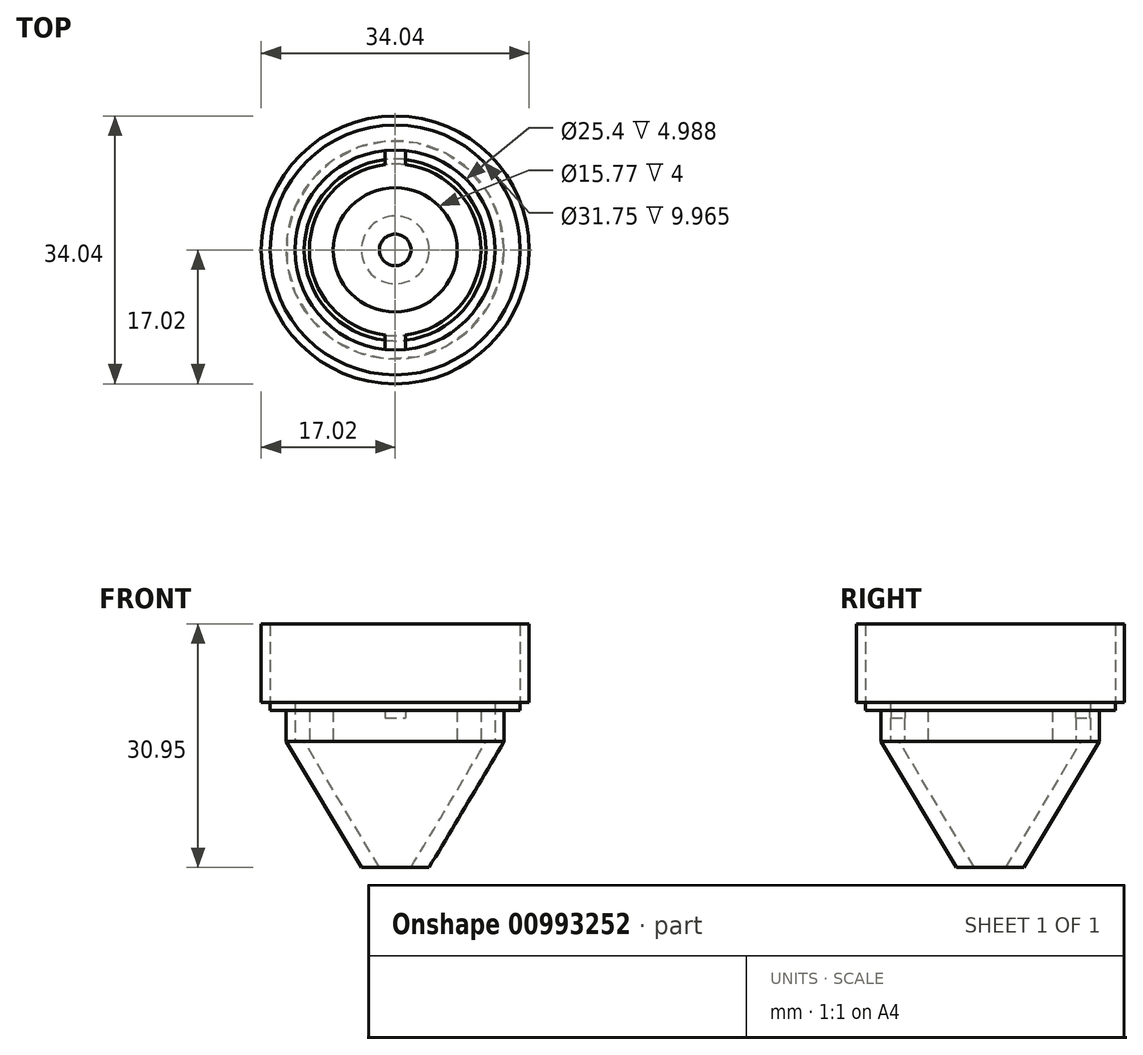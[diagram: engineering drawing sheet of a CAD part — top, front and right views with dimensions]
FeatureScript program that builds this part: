
annotation { "Feature Type Name" : "Feature", "Feature Type Description" : "" }
export const myFeature = defineFeature(function(context is Context, id is Id, definition is map)
    precondition{}
    {
        {
            var Q0;
            Q0=qCreatedBy(makeId("Top.planeOp"),FACE);
            var sketch = newSketch(context, id + "F0", { "sketchPlane" : qUnion([Q0])});
            skCircle(sketch, "E0", {"center": v(0, 0) * mm, "radius": 7.89 * mm});
            skArc(sketch, "E1", {"start": v(1.3, -10.82) * mm, "mid": v(10.9, 0) * mm, "end": v(1.3, 10.82) * mm});
            skArc(sketch, "E2", {"start": v(1.3, -12.63) * mm, "mid": v(12.7, 0) * mm, "end": v(1.3, 12.63) * mm});
            skCircle(sketch, "E3", {"center": v(0, 0) * mm, "radius": 13.85 * mm});
            skLineSegment(sketch, "E4", {"start": v(-1.3, -12.63) * mm, "end": v(-1.3, -10.82) * mm});
            skLineSegment(sketch, "E5.MirrorCS", {"start": v(1.3, -12.63) * mm, "end": v(1.3, -10.82) * mm});
            skLineSegment(sketch, "E6.trimOffspring", {"start": v(-1.3, 10.82) * mm, "end": v(-1.3, 12.63) * mm});
            skLineSegment(sketch, "E7.trimOffspring", {"start": v(1.3, 10.82) * mm, "end": v(1.3, 12.63) * mm});
            skArc(sketch, "E8.trimOffspring", {"start": v(-1.3, 10.82) * mm, "mid": v(-10.9, 0) * mm, "end": v(-1.3, -10.82) * mm});
            skArc(sketch, "E9.trimOffspring", {"start": v(-1.3, 12.63) * mm, "mid": v(-12.7, 0) * mm, "end": v(-1.3, -12.63) * mm});
            skSolve(sketch);
        }
        {
            var Q0;
            Q0=qSketchRegion(id+"F0",true);
            extrude(context, id + "F1", {"entities" : qUnion([Q0]), "depth" : 4 * mm, "offsetDistance" : 25.4 * mm});
        }
        {
            var Q0;
            Q0=qCreatedBy(makeId("Top.planeOp"),FACE);
            var sketch = newSketch(context, id + "F2", { "sketchPlane" : qUnion([Q0])});
            skCircle(sketch, "E10", {"center": v(0, 0) * mm, "radius": 12.7 * mm});
            skCircle(sketch, "E11", {"center": v(0, 0) * mm, "radius": 10.9 * mm});
            skSolve(sketch);
        }
        {
            var Q0;
            Q0=qSketchRegion(id+"F2",true);
            extrude(context, id + "F3", {"entities" : qUnion([Q0]), "depth" : 3 * mm, "offsetDistance" : 25.4 * mm});
        }
        {
            var Q0;
            Q0=makeQuery(id+"F3.opExtrude","SWEPT_BODY",BODY,{"disambiguationData":[OSD([sQuery(id+"F2.wireOp",EDGE,"E10"),sQuery(id+"F2.wireOp",EDGE,"E11")])]});
            var Q1;
            Q1=makeQuery(id+"F1.opExtrude","SWEPT_BODY",BODY,{"disambiguationData":[OSD([sQuery(id+"F0.wireOp",EDGE,"E0"),sQuery(id+"F0.wireOp",EDGE,"E1"),sQuery(id+"F0.wireOp",EDGE,"E2"),sQuery(id+"F0.wireOp",EDGE,"E3"),sQuery(id+"F0.wireOp",EDGE,"E4"),sQuery(id+"F0.wireOp",EDGE,"E5.MirrorCS"),sQuery(id+"F0.wireOp",EDGE,"E6.trimOffspring"),sQuery(id+"F0.wireOp",EDGE,"E7.trimOffspring"),sQuery(id+"F0.wireOp",EDGE,"E8.trimOffspring"),sQuery(id+"F0.wireOp",EDGE,"E9.trimOffspring")])]});
            booleanBodies(context, id + "F4", {"operationType" : BooleanOperationType.SUBTRACTION, "tools" : qUnion([Q0]), "targets" : qUnion([Q1])});
        }
        {
            var Q0;
            Q0=qCreatedBy(makeId("Top.planeOp"),FACE);
            cPlane(context, id + "F5", {"entities" : qUnion([Q0]), "cplaneType" : CPlaneType.OFFSET, "offset" : 4 * mm, "width" : 152.4 * mm, "height" : 152.4 * mm});
        }
        {
            var Q0;
            Q0=qCreatedBy(id+"F5.planeOp",FACE);
            var sketch = newSketch(context, id + "F6", { "sketchPlane" : qUnion([Q0])});
            skCircle(sketch, "E12", {"center": v(0, 0) * mm, "radius": 15.88 * mm});
            skCircle(sketch, "E13", {"center": v(0, 0) * mm, "radius": 12.7 * mm});
            skSolve(sketch);
        }
        {
            var Q0;
            Q0=qSketchRegion(id+"F6",true);
            extrude(context, id + "F7", {"entities" : qUnion([Q0]), "operationType" : NewBodyOperationType.ADD, "depth" : 1 * mm, "offsetDistance" : 25.4 * mm});
        }
        {
            var Q0;
            Q0=qCreatedBy(makeId("Top.planeOp"),FACE);
            cPlane(context, id + "F8", {"entities" : qUnion([Q0]), "cplaneType" : CPlaneType.OFFSET, "offset" : 4.95 * mm, "width" : 152.4 * mm, "height" : 152.4 * mm});
        }
        {
            var Q0;
            Q0=qCreatedBy(id+"F8.planeOp",FACE);
            var sketch = newSketch(context, id + "F9", { "sketchPlane" : qUnion([Q0])});
            skCircle(sketch, "E14", {"center": v(0, 0) * mm, "radius": 15.88 * mm});
            skCircle(sketch, "E15", {"center": v(0, 0) * mm, "radius": 17.02 * mm});
            skSolve(sketch);
        }
        {
            var Q0;
            Q0 = qSketchRegion(id + "F9", true);
            extrude(context, id + "F10", {"entities" : qUnion([Q0]), "operationType" : NewBodyOperationType.ADD, "depth" : 10 * mm, "offsetDistance" : 25.4 * mm});
        }
        {
            var Q0;
            Q0=qCreatedBy(makeId("Front.planeOp"),FACE);
            var sketch = newSketch(context, id + "F11", { "sketchPlane" : qUnion([Q0])});
            skLineSegment(sketch, "E16", {"start": v(0, 0) * mm, "end": v(0, -16) * mm});
            skLineSegment(sketch, "E17", {"start": v(-13.85, 0) * mm, "end": v(-11.55, 0) * mm});
            skLineSegment(sketch, "E18", {"start": v(-11.55, 0) * mm, "end": v(-2, -16) * mm});
            skLineSegment(sketch, "E19", {"start": v(-2, -16) * mm, "end": v(-4.3, -16) * mm});
            skLineSegment(sketch, "E20", {"start": v(-13.85, 0) * mm, "end": v(-4.3, -16) * mm});
            skSolve(sketch);
        }
        {
            var Q0;
            Q0=makeQuery(id+"F11.imprint","IMPRINT",FACE,{"disambiguationData":[TD([[makeQuery(id+"F11.imprint","IMPRINT",EDGE,{"derivedFrom":sQuery(id+"F11.wireOp",EDGE,"E17")}),-1.0]])]});
            var Q1;
            Q1=sQuery(id+"F11.wireOp",EDGE,"E16");
            revolve(context, id + "F12", {"operationType" : NewBodyOperationType.ADD, "surfaceOperationType" : NewSurfaceOperationType.NEW, "entities" : qUnion([Q0]), "axis" : qUnion([Q1]), "revolveType" : RevolveType.FULL});
        }
    });
